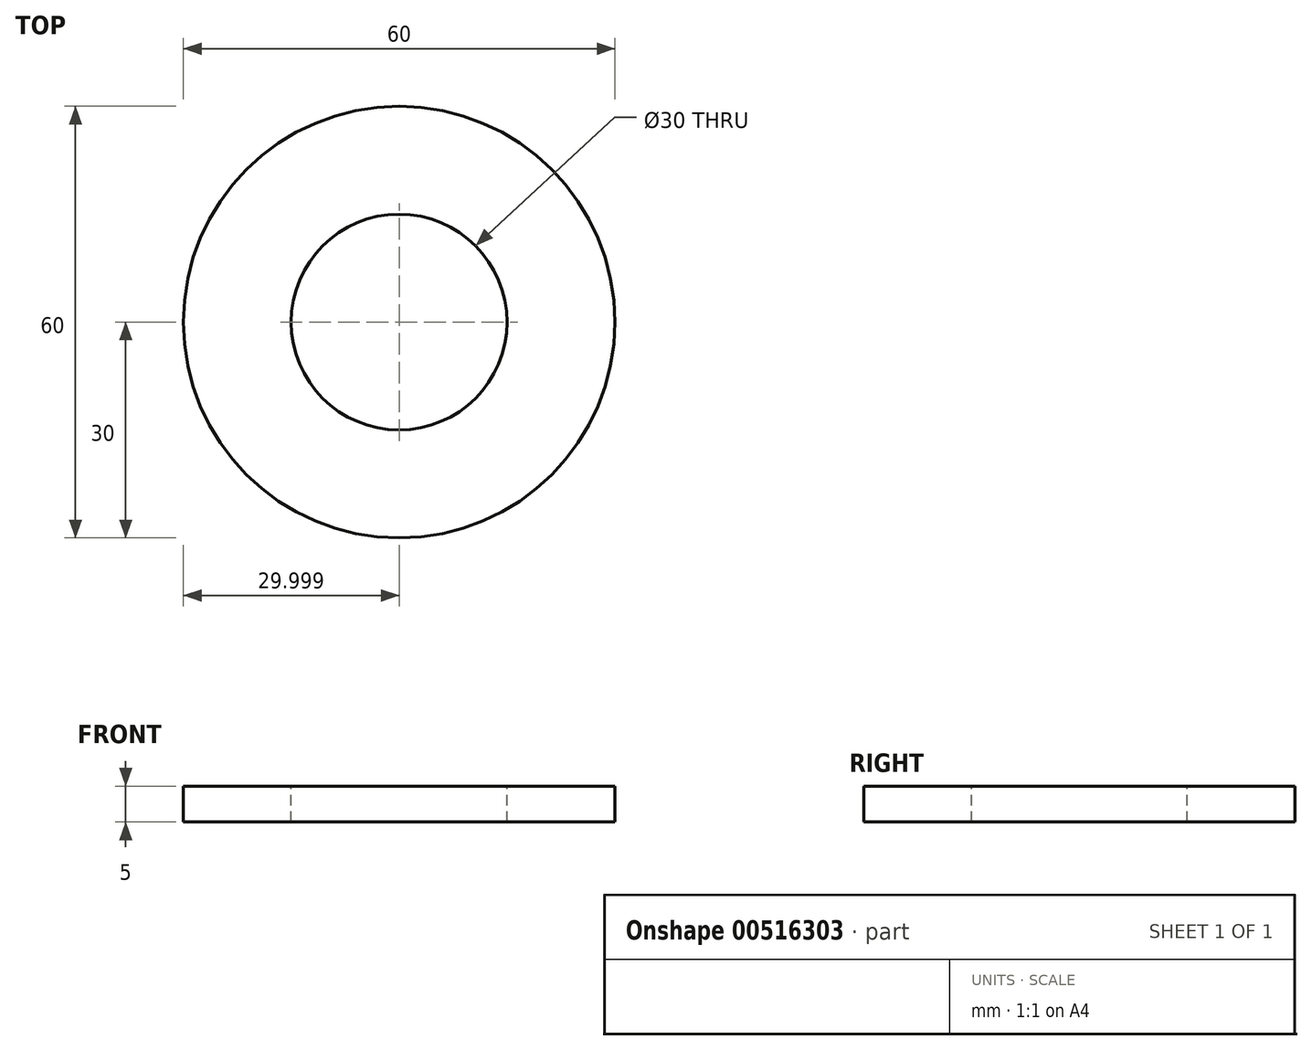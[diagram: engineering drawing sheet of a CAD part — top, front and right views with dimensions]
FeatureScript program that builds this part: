
annotation { "Feature Type Name" : "Feature", "Feature Type Description" : "" }
export const myFeature = defineFeature(function(context is Context, id is Id, definition is map)
    precondition{}
    {
        {
            var Q0;
            Q0=qCreatedBy(makeId("Top.planeOp"),FACE);
            var sketch = newSketch(context, id + "F0", { "sketchPlane" : qUnion([Q0])});
            skCircle(sketch, "E0", {"center": v(0, 0) * mm, "radius": 17 * mm});
            skSolve(sketch);
        }
        {
            var Q0;
            Q0=qCreatedBy(makeId("Top.planeOp"),FACE);
            var sketch = newSketch(context, id + "F1", { "sketchPlane" : qUnion([Q0])});
            skLineSegment(sketch, "E1.bottom", {"start": v(-12.88, 37) * mm, "end": v(13.12, 37) * mm});
            skLineSegment(sketch, "E1.top", {"start": v(-12.88, 27) * mm, "end": v(13.12, 27) * mm});
            skLineSegment(sketch, "E1.left", {"start": v(-14.88, 35) * mm, "end": v(-14.88, 29) * mm});
            skLineSegment(sketch, "E1.right", {"start": v(15.12, 35) * mm, "end": v(15.12, 29) * mm});
            skPoint(sketch, "E2.visualSharp", {"position": v(15.12, 37) * mm});
            skArc(sketch, "E2.filletArc", {"start": v(15.12, 35) * mm, "mid": v(14.53, 36.41) * mm, "end": v(13.12, 37) * mm});
            skPoint(sketch, "E3.visualSharp", {"position": v(15.12, 27) * mm});
            skArc(sketch, "E3.filletArc", {"start": v(13.12, 27) * mm, "mid": v(14.53, 27.59) * mm, "end": v(15.12, 29) * mm});
            skPoint(sketch, "E4.visualSharp", {"position": v(-14.88, 27) * mm});
            skArc(sketch, "E4.filletArc", {"start": v(-14.88, 29) * mm, "mid": v(-14.3, 27.59) * mm, "end": v(-12.88, 27) * mm});
            skPoint(sketch, "E5.visualSharp", {"position": v(-14.88, 37) * mm});
            skArc(sketch, "E5.filletArc", {"start": v(-12.88, 37) * mm, "mid": v(-14.3, 36.41) * mm, "end": v(-14.88, 35) * mm});
            skSolve(sketch);
        }
        {
            var Q0;
            Q0=qCreatedBy(makeId("Top.planeOp"),FACE);
            var sketch = newSketch(context, id + "F2", { "sketchPlane" : qUnion([Q0])});
            skLineSegment(sketch, "E6.bottom", {"start": v(2, 7.91) * mm, "end": v(88, 7.91) * mm});
            skLineSegment(sketch, "E6.top", {"start": v(2, -7.09) * mm, "end": v(88, -7.09) * mm});
            skLineSegment(sketch, "E6.left", {"start": v(0, 5.91) * mm, "end": v(0, -5.09) * mm});
            skLineSegment(sketch, "E6.right", {"start": v(90, 5.91) * mm, "end": v(90, -5.09) * mm});
            skPoint(sketch, "E7.visualSharp", {"position": v(90, 7.91) * mm});
            skArc(sketch, "E7.filletArc", {"start": v(90, 5.91) * mm, "mid": v(89.41, 7.33) * mm, "end": v(88, 7.91) * mm});
            skPoint(sketch, "E8.visualSharp", {"position": v(90, -7.09) * mm});
            skArc(sketch, "E8.filletArc", {"start": v(88, -7.09) * mm, "mid": v(89.41, -6.5) * mm, "end": v(90, -5.09) * mm});
            skPoint(sketch, "E9.visualSharp", {"position": v(0, -7.09) * mm});
            skArc(sketch, "E9.filletArc", {"start": v(0, -5.09) * mm, "mid": v(0.59, -6.5) * mm, "end": v(2, -7.09) * mm});
            skPoint(sketch, "E10.visualSharp", {"position": v(0, 7.91) * mm});
            skArc(sketch, "E10.filletArc", {"start": v(2, 7.91) * mm, "mid": v(0.59, 7.33) * mm, "end": v(0, 5.91) * mm});
            skSolve(sketch);
        }
        {
            var Q0;
            Q0=qCreatedBy(makeId("Top.planeOp"),FACE);
            var sketch = newSketch(context, id + "F3", { "sketchPlane" : qUnion([Q0])});
            skCircle(sketch, "E11", {"center": v(-65.22, 0) * mm, "radius": 30 * mm});
            skSolve(sketch);
        }
        {
            var Q0;
            Q0=qCreatedBy(makeId("Top.planeOp"),FACE);
            var sketch = newSketch(context, id + "F4", { "sketchPlane" : qUnion([Q0])});
            skCircle(sketch, "E12", {"center": v(-65.22, 0) * mm, "radius": 15 * mm});
            skSolve(sketch);
        }
        {
            var Q0;
            Q0 = qSketchRegion(id + "F3", true);
            extrude(context, id + "F5", {"entities" : qUnion([Q0]), "oppositeDirection" : true, "depth" : 5 * mm, "offsetDistance" : 25 * mm});
        }
        {
            var Q0;
            Q0 = qSketchRegion(id + "F4", true);
            extrude(context, id + "F6", {"entities" : qUnion([Q0]), "operationType" : NewBodyOperationType.REMOVE, "endBound" : BoundingType.THROUGH_ALL, "oppositeDirection" : true, "depth" : 25 * mm, "offsetDistance" : 25 * mm});
        }
    });
